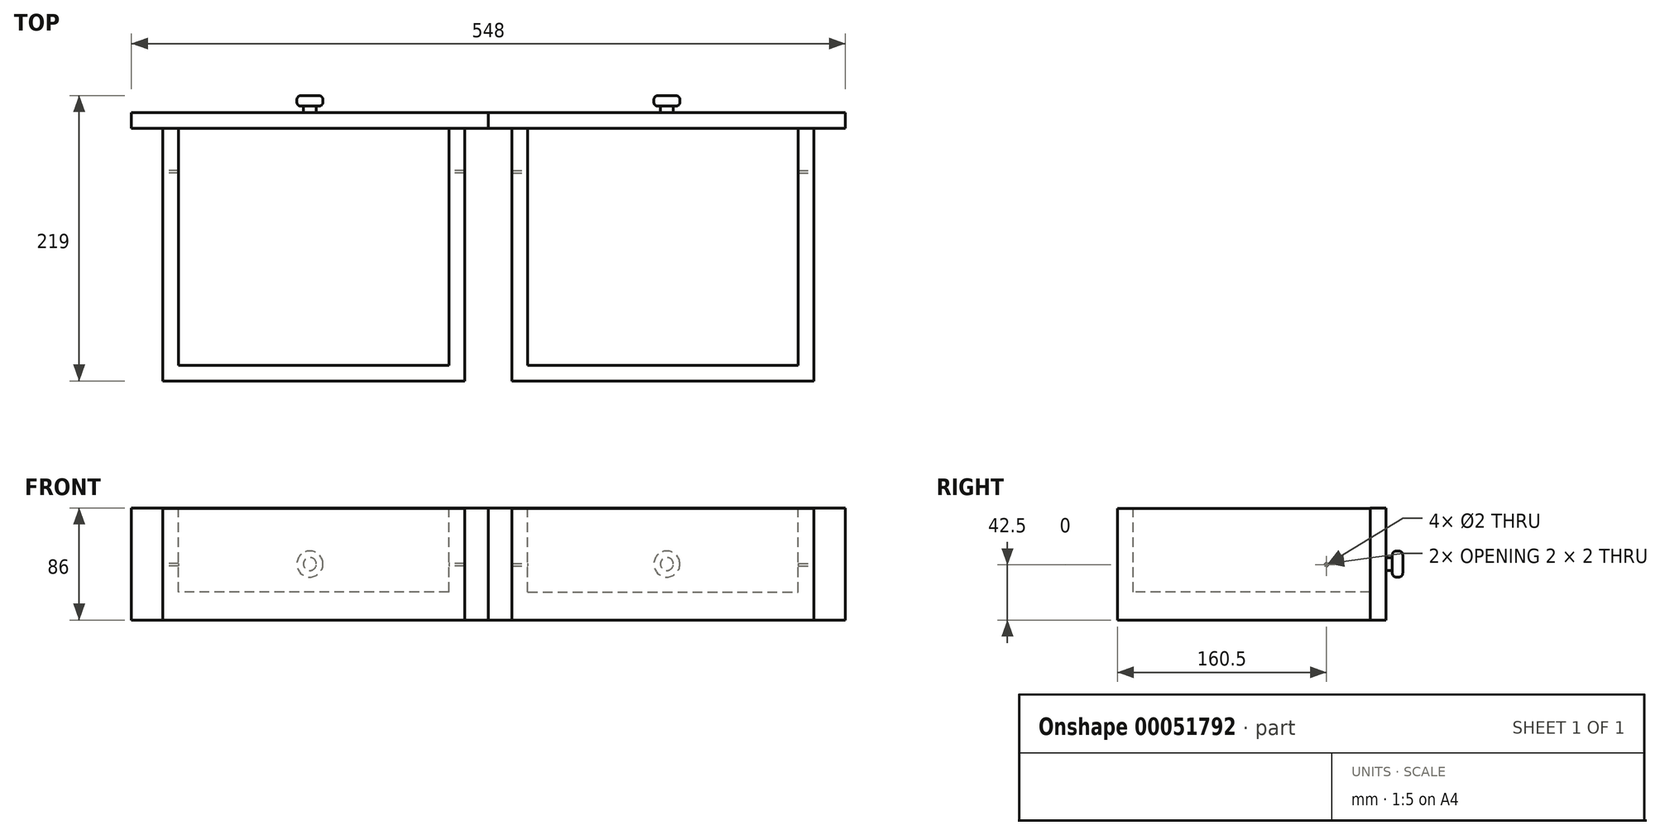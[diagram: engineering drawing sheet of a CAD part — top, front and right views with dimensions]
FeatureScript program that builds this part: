
annotation { "Feature Type Name" : "Feature", "Feature Type Description" : "" }
export const myFeature = defineFeature(function(context is Context, id is Id, definition is map)
    precondition{}
    {
        {
            var Q0;
            Q0=qCreatedBy(makeId("Front.planeOp"),FACE);
            var sketch = newSketch(context, id + "F0", { "sketchPlane" : qUnion([Q0])});
            skLineSegment(sketch, "E0.bottom", {"start": v(-137, 43) * mm, "end": v(137, 43) * mm});
            skLineSegment(sketch, "E0.top", {"start": v(-137, -43) * mm, "end": v(137, -43) * mm});
            skLineSegment(sketch, "E0.left", {"start": v(-137, 43) * mm, "end": v(-137, -43) * mm});
            skLineSegment(sketch, "E0.right", {"start": v(137, 43) * mm, "end": v(137, -43) * mm});
            skSolve(sketch);
        }
        {
            var Q0;
            Q0=makeQuery(id+"F0.imprint","IMPRINT",FACE,{"disambiguationData":[TD([[makeQuery(id+"F0.imprint","IMPRINT",EDGE,{"derivedFrom":sQuery(id+"F0.wireOp",EDGE,"E0.bottom")}),-1.0]])]});
            extrude(context, id + "F1", {"entities" : qUnion([Q0]), "depth" : 12 * mm});
        }
        {
            var Q0;
            Q0=makeQuery(id+"F1.opExtrude","CAP_FACE",FACE,{"disambiguationData":[OSD([sQuery(id+"F0.wireOp",EDGE,"E0.bottom"),sQuery(id+"F0.wireOp",EDGE,"E0.top"),sQuery(id+"F0.wireOp",EDGE,"E0.left"),sQuery(id+"F0.wireOp",EDGE,"E0.right")])],"isStart":false});
            var sketch = newSketch(context, id + "F2", { "sketchPlane" : qUnion([Q0])});
            skLineSegment(sketch, "E1.bottom", {"start": v(-118.8, 42.5) * mm, "end": v(112.8, 42.5) * mm});
            skLineSegment(sketch, "E1.top", {"start": v(-118.8, -43) * mm, "end": v(112.8, -43) * mm});
            skLineSegment(sketch, "E1.left", {"start": v(-118.8, 42.5) * mm, "end": v(-118.8, -43) * mm});
            skLineSegment(sketch, "E1.right", {"start": v(112.8, 42.5) * mm, "end": v(112.8, -43) * mm});
            skSolve(sketch);
        }
        {
            var Q0;
            Q0=makeQuery(id+"F2.imprint","IMPRINT",FACE,{"disambiguationData":[TD([[makeQuery(id+"F2.imprint","IMPRINT",EDGE,{"derivedFrom":sQuery(id+"F2.wireOp",EDGE,"E1.bottom")}),-1.0]])]});
            extrude(context, id + "F3", {"entities" : qUnion([Q0]), "operationType" : NewBodyOperationType.ADD, "depth" : 194 * mm});
        }
        {
            var Q0;
            Q0=makeQuery(id+"F3.opExtrude","SWEPT_FACE",FACE,{"disambiguationData":[OSD([sQuery(id+"F2.wireOp",EDGE,"E1.bottom")])]});
            var sketch = newSketch(context, id + "F4", { "sketchPlane" : qUnion([Q0])});
            skLineSegment(sketch, "E2.bottom", {"start": v(100.8, -12) * mm, "end": v(-106.8, -12) * mm});
            skLineSegment(sketch, "E2.top", {"start": v(100.8, -194) * mm, "end": v(-106.8, -194) * mm});
            skLineSegment(sketch, "E2.left", {"start": v(100.8, -12) * mm, "end": v(100.8, -194) * mm});
            skLineSegment(sketch, "E2.right", {"start": v(-106.8, -12) * mm, "end": v(-106.8, -194) * mm});
            skSolve(sketch);
        }
        {
            var Q0;
            Q0=makeQuery(id+"F4.imprint","IMPRINT",FACE,{"disambiguationData":[TD([[makeQuery(id+"F4.imprint","IMPRINT",EDGE,{"derivedFrom":sQuery(id+"F4.wireOp",EDGE,"E2.bottom")}),-1.0]])]});
            extrude(context, id + "F5", {"entities" : qUnion([Q0]), "operationType" : NewBodyOperationType.REMOVE, "oppositeDirection" : true, "depth" : 64 * mm});
        }
        {
            var Q0;
            Q0=makeQuery(id+"F1.opExtrude","CAP_FACE",FACE,{"disambiguationData":[OSD([sQuery(id+"F0.wireOp",EDGE,"E0.bottom"),sQuery(id+"F0.wireOp",EDGE,"E0.top"),sQuery(id+"F0.wireOp",EDGE,"E0.left"),sQuery(id+"F0.wireOp",EDGE,"E0.right")])],"isStart":true});
            var sketch = newSketch(context, id + "F6", { "sketchPlane" : qUnion([Q0])});
            skCircle(sketch, "E3", {"center": v(0, 0) * mm, "radius": 5 * mm});
            skSolve(sketch);
        }
        {
            var Q0;
            Q0=makeQuery(id+"F6.imprint","IMPRINT",FACE,{"disambiguationData":[TD([[makeQuery(id+"F6.imprint","IMPRINT",EDGE,{"derivedFrom":sQuery(id+"F6.wireOp",EDGE,"E3")}),1.0]])]});
            extrude(context, id + "F7", {"entities" : qUnion([Q0]), "operationType" : NewBodyOperationType.ADD, "depth" : 5 * mm});
        }
        {
            var Q0;
            Q0=makeQuery(id+"F7.opExtrude","CAP_FACE",FACE,{"disambiguationData":[OSD([sQuery(id+"F6.wireOp",EDGE,"E3")])],"isStart":false});
            var sketch = newSketch(context, id + "F13", { "sketchPlane" : qUnion([Q0])});
            skCircle(sketch, "E4", {"center": v(0, 0) * mm, "radius": 10 * mm});
            skSolve(sketch);
        }
        {
            var Q0;
            Q0=makeQuery(id+"F13.imprint","IMPRINT",FACE,{"disambiguationData":[TD([[makeQuery(id+"F13.imprint","IMPRINT",EDGE,{"derivedFrom":sQuery(id+"F13.wireOp",EDGE,"E4")}),1.0]])]});
            var Q1;
            Q1=makeQuery(id+"F13.imprint","IMPRINT",FACE,{"disambiguationData":[TD([[makeQuery(id+"F13.imprint","IMPRINT",EDGE,{"derivedFrom":makeQuery(id+"F7.opExtrude","CAP_EDGE",EDGE,{"disambiguationData":[OSD([sQuery(id+"F6.wireOp",EDGE,"E3")])],"isStart":false})}),1.0]])]});
            extrude(context, id + "F8", {"entities" : qUnion([Q0, Q1]), "operationType" : NewBodyOperationType.ADD, "depth" : 8 * mm});
        }
        {
            var Q0;
            Q0=makeQuery(id+"F8.opExtrude","CAP_EDGE",EDGE,{"disambiguationData":[OSD([sQuery(id+"F13.wireOp",EDGE,"E4")])],"isStart":false});
            var Q1;
            Q1=makeQuery(id+"F8.opExtrude","CAP_EDGE",EDGE,{"disambiguationData":[OSD([sQuery(id+"F13.wireOp",EDGE,"E4")])],"isStart":true});
            fillet(context, id + "F14", {"entities" : qUnion([Q0, Q1]), "radius" : 3 * mm, "tangentPropagation" : true, "allowEdgeOverflow" : false});
        }
        {
            var Q0;
            Q0=makeQuery(id+"F3.opExtrude","SWEPT_FACE",FACE,{"disambiguationData":[OSD([sQuery(id+"F2.wireOp",EDGE,"E1.right")])]});
            var sketch = newSketch(context, id + "F9", { "sketchPlane" : qUnion([Q0])});
            skPoint(sketch, "E5", {"position": v(-45.5, -0.5) * mm});
            skSolve(sketch);
        }
        {
            var Q0;
            Q0=sQuery(id+"F9.wireOp",VERTEX,"E5");
            var Q1;
            Q1=makeQuery(id+"F1.opExtrude","SWEPT_BODY",BODY,{"disambiguationData":[OSD([sQuery(id+"F0.wireOp",EDGE,"E0.bottom"),sQuery(id+"F0.wireOp",EDGE,"E0.top"),sQuery(id+"F0.wireOp",EDGE,"E0.left"),sQuery(id+"F0.wireOp",EDGE,"E0.right")])]});
            hole(context, id + "F10", {"style" : HoleStyle.SIMPLE, "endStyle" : HoleEndStyle.THROUGH, "holeDiameter" : 2 * mm, "locations" : qUnion([Q0]), "scope" : qUnion([Q1]), "isTappedThrough" : true});
        }
        {
            var Q0;
            Q0=makeQuery(id+"F1.opExtrude","SWEPT_FACE",FACE,{"disambiguationData":[OSD([sQuery(id+"F0.wireOp",EDGE,"E0.left")])]});
            cPlane(context, id + "F11", {"entities" : qUnion([Q0]), "cplaneType" : CPlaneType.OFFSET, "offset" : 0 * mm, "width" : 150 * mm, "height" : 150 * mm});
        }
        {
            var Q0;
            Q0=makeQuery(id+"F1.opExtrude","SWEPT_BODY",BODY,{"disambiguationData":[OSD([sQuery(id+"F0.wireOp",EDGE,"E0.bottom"),sQuery(id+"F0.wireOp",EDGE,"E0.top"),sQuery(id+"F0.wireOp",EDGE,"E0.left"),sQuery(id+"F0.wireOp",EDGE,"E0.right")])]});
            var Q1;
            Q1=qCreatedBy(id+"F11.planeOp",FACE);
            mirror(context, id + "F12", {"entities" : qUnion([Q0]), "mirrorPlane" : qUnion([Q1])});
        }
    });
